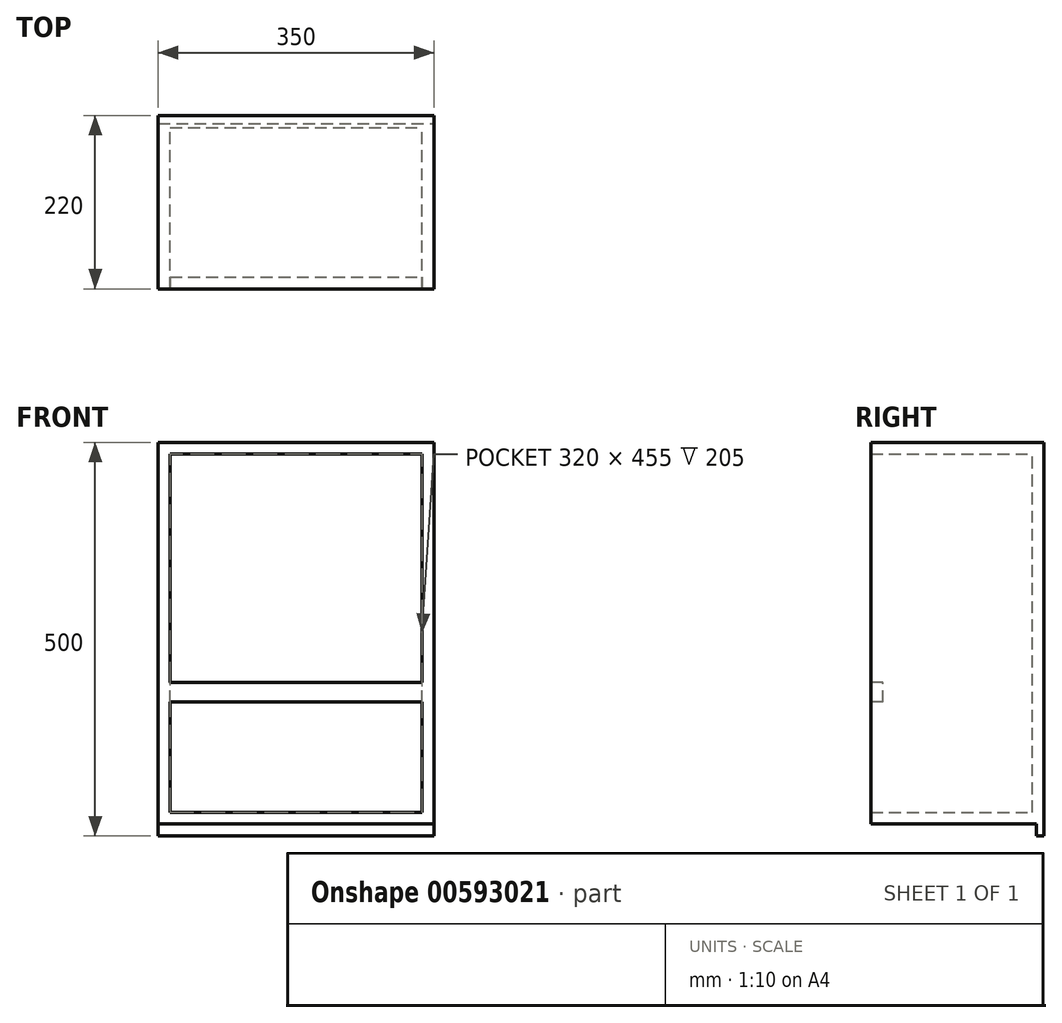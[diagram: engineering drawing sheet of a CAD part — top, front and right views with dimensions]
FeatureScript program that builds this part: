
annotation { "Feature Type Name" : "Feature", "Feature Type Description" : "" }
export const myFeature = defineFeature(function(context is Context, id is Id, definition is map)
    precondition{}
    {
        {
            var Q0;
            Q0=qCreatedBy(makeId("Front.planeOp"),FACE);
            var sketch = newSketch(context, id + "F0", { "sketchPlane" : qUnion([Q0])});
            skLineSegment(sketch, "E0.bottom", {"start": v(0, 0) * mm, "end": v(350, 0) * mm});
            skLineSegment(sketch, "E0.top", {"start": v(0, 485) * mm, "end": v(350, 485) * mm});
            skLineSegment(sketch, "E0.left", {"start": v(0, 0) * mm, "end": v(0, 485) * mm});
            skLineSegment(sketch, "E0.right", {"start": v(350, 0) * mm, "end": v(350, 485) * mm});
            skSolve(sketch);
        }
        {
            var Q0;
            Q0 = qSketchRegion(id + "F0", true);
            extrude(context, id + "F1", {"entities" : qUnion([Q0]), "depth" : 220 * mm, "offsetDistance" : 25 * mm});
        }
        {
            var Q0;
            Q0=makeQuery(id+"F1.opExtrude","CAP_FACE",FACE,{"disambiguationData":[OSD([sQuery(id+"F0.wireOp",EDGE,"E0.bottom"),sQuery(id+"F0.wireOp",EDGE,"E0.top"),sQuery(id+"F0.wireOp",EDGE,"E0.left"),sQuery(id+"F0.wireOp",EDGE,"E0.right")])],"isStart":false});
            shell(context, id + "F2", {"entities" : qUnion([Q0]), "thickness" : 15 * mm});
        }
        {
            var Q0;
            Q0=makeQuery(id+"F1.opExtrude","CAP_FACE",FACE,{"disambiguationData":[OSD([sQuery(id+"F0.wireOp",EDGE,"E0.bottom"),sQuery(id+"F0.wireOp",EDGE,"E0.top"),sQuery(id+"F0.wireOp",EDGE,"E0.left"),sQuery(id+"F0.wireOp",EDGE,"E0.right")])],"isStart":false});
            var sketch = newSketch(context, id + "F3", { "sketchPlane" : qUnion([Q0])});
            skLineSegment(sketch, "E1.bottom", {"start": v(15, 180) * mm, "end": v(335, 180) * mm});
            skLineSegment(sketch, "E1.top", {"start": v(15, 155) * mm, "end": v(335, 155) * mm});
            skLineSegment(sketch, "E1.left", {"start": v(15, 180) * mm, "end": v(15, 155) * mm});
            skLineSegment(sketch, "E1.right", {"start": v(335, 180) * mm, "end": v(335, 155) * mm});
            skSolve(sketch);
        }
        {
            var Q0;
            Q0 = qSketchRegion(id + "F3", true);
            extrude(context, id + "F4", {"entities" : qUnion([Q0]), "operationType" : NewBodyOperationType.ADD, "oppositeDirection" : true, "depth" : 15 * mm, "offsetDistance" : 25 * mm});
        }
        {
            var Q0;
            Q0=makeQuery(id+"F1.opExtrude","SWEPT_FACE",FACE,{"disambiguationData":[OSD([sQuery(id+"F0.wireOp",EDGE,"E0.bottom")])]});
            var sketch = newSketch(context, id + "F5", { "sketchPlane" : qUnion([Q0])});
            skLineSegment(sketch, "E2.bottom", {"start": v(0, 0) * mm, "end": v(350, 0) * mm});
            skLineSegment(sketch, "E2.top", {"start": v(0, 10) * mm, "end": v(350, 10) * mm});
            skLineSegment(sketch, "E2.left", {"start": v(0, 0) * mm, "end": v(0, 10) * mm});
            skLineSegment(sketch, "E2.right", {"start": v(350, 0) * mm, "end": v(350, 10) * mm});
            skSolve(sketch);
        }
        {
            var Q0;
            Q0 = qSketchRegion(id + "F5", true);
            extrude(context, id + "F6", {"entities" : qUnion([Q0]), "operationType" : NewBodyOperationType.ADD, "depth" : 15 * mm, "offsetDistance" : 25 * mm});
        }
    });
